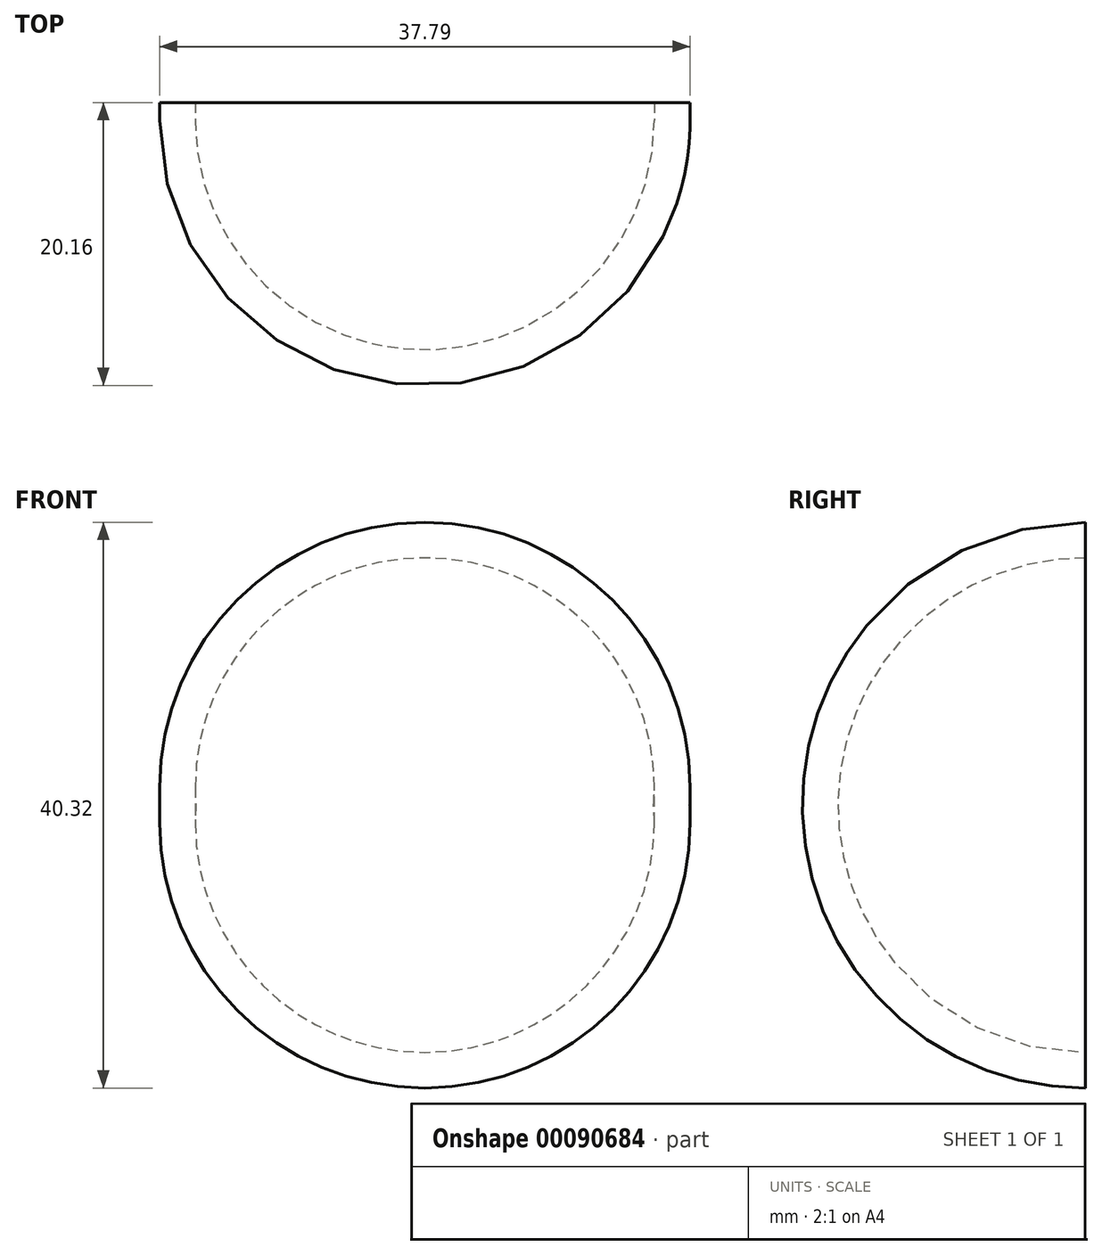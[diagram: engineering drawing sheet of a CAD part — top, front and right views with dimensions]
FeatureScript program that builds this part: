
annotation { "Feature Type Name" : "Feature", "Feature Type Description" : "" }
export const myFeature = defineFeature(function(context is Context, id is Id, definition is map)
    precondition{}
    {
        {
            var Q0;
            Q0=qCreatedBy(makeId("Front.planeOp"),FACE);
            var sketch = newSketch(context, id + "F0", { "sketchPlane" : qUnion([Q0])});
            skArc(sketch, "E0", {"start": v(19.41, 0) * mm, "mid": v(0.57, 20.16) * mm, "end": v(-18.28, 0) * mm});
            skLineSegment(sketch, "E1", {"start": v(-18.28, 0) * mm, "end": v(19.41, 0) * mm});
            skSolve(sketch);
        }
        {
            var Q0;
            Q0=makeQuery(id+"F0.imprint","IMPRINT",FACE,{"disambiguationData":[TD([[makeQuery(id+"F0.imprint","IMPRINT",EDGE,{"derivedFrom":sQuery(id+"F0.wireOp",EDGE,"E0")}),1.0]])]});
            var Q1;
            Q1=sQuery(id+"F0.wireOp",EDGE,"E1");
            revolve(context, id + "F1", {"entities" : qUnion([Q0]), "axis" : qUnion([Q1]), "revolveType" : RevolveType.ONE_DIRECTION, "angle" : 180 * degree});
        }
        {
            var Q0;
            Q0=makeQuery(id+"F1.opRevolve","CAP_FACE",FACE,{"disambiguationData":[OSD([sQuery(id+"F0.wireOp",EDGE,"E0"),sQuery(id+"F0.wireOp",EDGE,"E1")])],"isStart":false});
            shell(context, id + "F2", {"entities" : qUnion([Q0]), "thickness" : 2.54 * mm});
        }
    });
